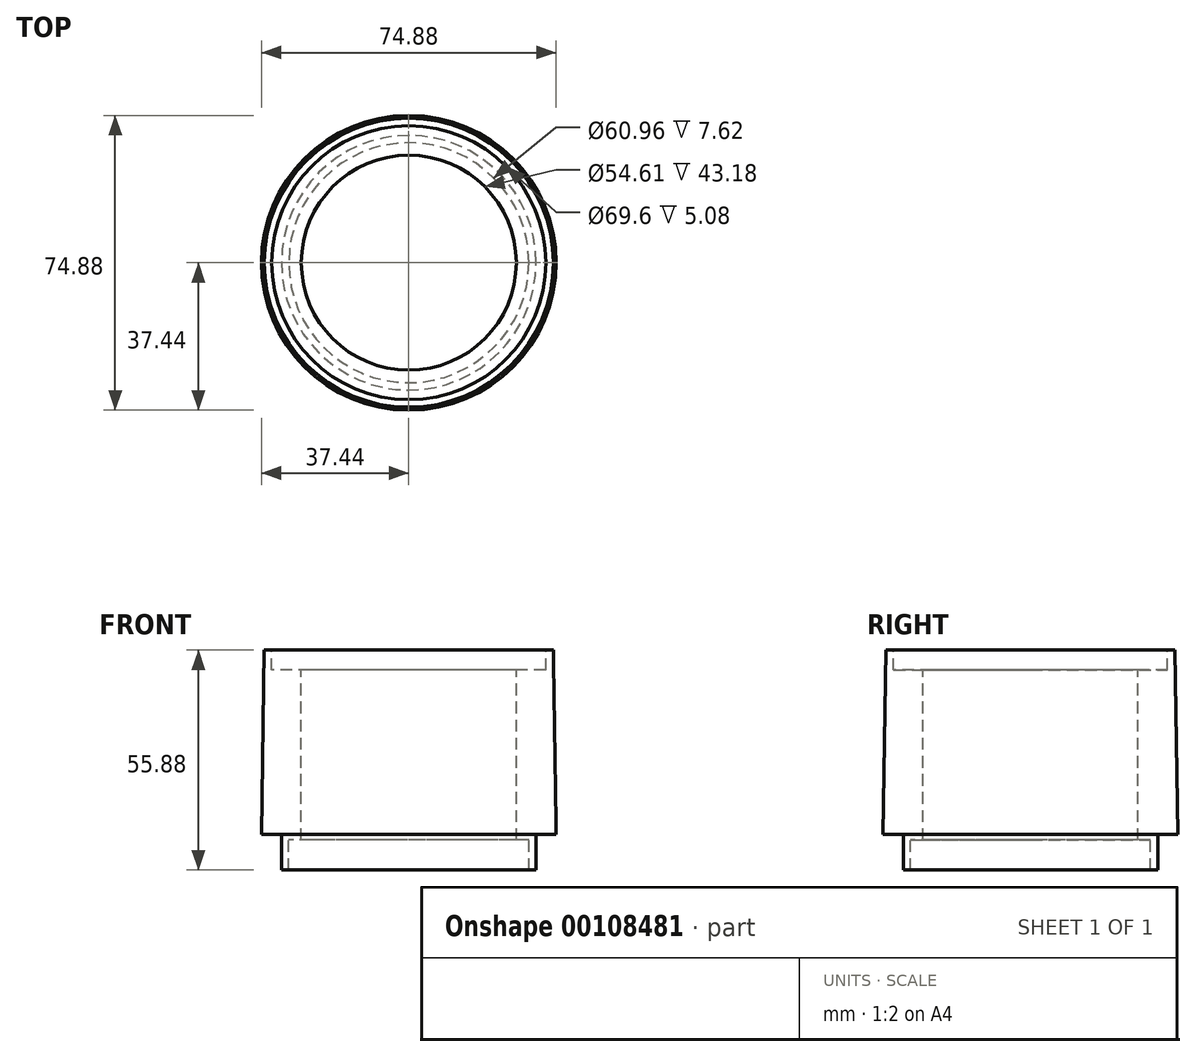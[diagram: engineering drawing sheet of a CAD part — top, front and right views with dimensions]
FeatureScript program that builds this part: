
annotation { "Feature Type Name" : "Feature", "Feature Type Description" : "" }
export const myFeature = defineFeature(function(context is Context, id is Id, definition is map)
    precondition{}
    {
        {
            var Q0;
            Q0=qCreatedBy(makeId("Front.planeOp"),FACE);
            var sketch = newSketch(context, id + "F0", { "sketchPlane" : qUnion([Q0])});
            skLineSegment(sketch, "E0", {"start": v(-32.34, 0) * mm, "end": v(-30.48, 0) * mm});
            skLineSegment(sketch, "E1", {"start": v(-36.71, 55.88) * mm, "end": v(-34.8, 55.88) * mm});
            skLineSegment(sketch, "E2", {"start": v(-34.8, 55.88) * mm, "end": v(-34.8, 50.8) * mm});
            skLineSegment(sketch, "E3", {"start": v(-34.8, 50.8) * mm, "end": v(-27.3, 50.8) * mm});
            skLineSegment(sketch, "E4", {"start": v(-30.48, 0) * mm, "end": v(-30.48, 7.62) * mm});
            skLineSegment(sketch, "E5", {"start": v(-30.48, 7.62) * mm, "end": v(-27.3, 7.62) * mm});
            skLineSegment(sketch, "E6", {"start": v(-37.44, 9.1) * mm, "end": v(-32.34, 9.1) * mm});
            skLineSegment(sketch, "E7", {"start": v(-32.34, 9.1) * mm, "end": v(-32.34, 0) * mm});
            skLineSegment(sketch, "E8", {"start": v(-27.3, 50.8) * mm, "end": v(-27.3, 7.62) * mm});
            skLineSegment(sketch, "E9", {"start": v(-36.71, 55.88) * mm, "end": v(-37.44, 9.1) * mm});
            skLineSegment(sketch, "E10", {"start": v(0, 73.78) * mm, "end": v(0, 0) * mm, "construction": true});
            skSolve(sketch);
        }
        {
            var Q0;
            Q0=qCreatedBy(makeId("Front.planeOp"),FACE);
            var sketch = newSketch(context, id + "F1", { "sketchPlane" : qUnion([Q0])});
            skLineSegment(sketch, "E11", {"start": v(0, 65.1) * mm, "end": v(0, 0) * mm, "construction": true});
            skSolve(sketch);
        }
        {
            var Q0;
            Q0=makeQuery(id+"F0.imprint","IMPRINT",FACE,{"disambiguationData":[TD([[makeQuery(id+"F0.imprint","IMPRINT",EDGE,{"derivedFrom":sQuery(id+"F0.wireOp",EDGE,"E0")}),1.0]])]});
            var Q1;
            Q1=sQuery(id+"F1.wireOp",EDGE,"E11");
            revolve(context, id + "F2", {"entities" : qUnion([Q0]), "axis" : qUnion([Q1]), "revolveType" : RevolveType.FULL});
        }
    });
